# Revit family: PRD_FrankeWS_Bths_CAMPUSBabyBathtub_CMPX0072_CMPX0073
name_source: partatom
category: Plumbing Fixtures
revit_build: Autodesk Revit 2018 (Build: 20190510_1515(x64)
units: mm (PartAtom-declared; Revit-internal decimal feet)

## family parameters
Cut with Voids When Loaded = Yes
Host = Face
OmniClass Number = 23.45.05.14.21
OmniClass Title = Bathtubs
Part Type = Normal
Room Calculation Point = No
Round Connector Dimension = Use Diameter
Shared = Yes

## types (2) — shared parameters
AssetType = Fixed
Category = Pr_40_20_06_08, Baths
DiameterNominal = 40  [stored 0.131234 ft]
DrainSize = 40 mm  [stored 0.131234 ft]
DurationUnit = year
Features = Chrome-nickel steel, satin finished surface, contents 10 L.
Finish = Satin finished
GeneralMaterial = PRD_AR_StainlessSteel_Rugged
GrossWeight = 9.00 kg
HasGrabHandles = FALSE
IfcExportAs = IfcSanitaryTerminalType
IfcExportType = BATH
Manufacturer = KWC Group AG
ManufacturerName = KWC Group AG
ManufacturerURL = www.kwc.com
Material = Stainless steel
MaterialCode = 1.4301 Chrome Nickel steel V2A
MaterialThickness = 1.20 mm
NBSDescription = Baths
NBSReference = 45-35-70/311
NetWeight = 8.55 kg
NominalDepth = 445 mm  [stored 1.45997 ft]
NominalHeight = 250 mm  [stored 0.82021 ft]
NominalWidth = 743 mm  [stored 2.43766 ft]
ProductInformation = https://pim.kwc.com
Size = 743 x 250 x 445 mm (W x H x D)
TailorMade = Yes
TypeOfMounting = Inset mounting
URL = www.kwc.com
Uniclass2015Code = Pr_40_20_06_08
Uniclass2015Title = Baths
Uniclass2015Version = Products v1.17
Version = 1
WarrantyDurationUnit = year
WasteSize = DN 40
zero-valued in all types: Default Elevation

## per-type parameters (varying)
| type | BIMObjectName | Description | ModelNumber | Name |
| CMPX0072 | PRD_AR_Baths_CAMPUSBabyBathtub_CMPX0072 | Baby bathtub, installed from above, made of chrome-nickel steel, satin finished surface, material thickness 1.2 mm, waste and overflow fitting with plug waste set DN 40, contents 10 L. Dimensions 743 x 250 x 445 mm (W x H x D). Bowl dimensions 700 x 250 x 400 mm (W x H x D). | 2000111231 | CAMPUS Baby bathtub CMPX0072 |
| CMPX0073 | PRD_AR_Baths_CAMPUSBabyBathtub_CMPX0073 | Baby bathtub, installed from above, made of chrome-nickel steel, satin finished surface, material thickness 1.2 mm, waste and overflow with eccentric waste and overflow fitting set DN 40, contents 10 L. Dimensions 743 x 250 x 445 mm (W x H x D). Bowl dimensions 700 x 250 x 400 mm (W x H x D). | 2000111232 | CAMPUS Baby bathtub CMPX0073 |

note: column(s) folded — value = type name in every type: Model, ModelReference

note: [stored X ft] marks values corroborated as IEEE doubles in the binary element streams (Revit-internal decimal feet)

## geometry (parser evidence)
native form markers: Sweep x5
no freeform markers — native parametric forms only
